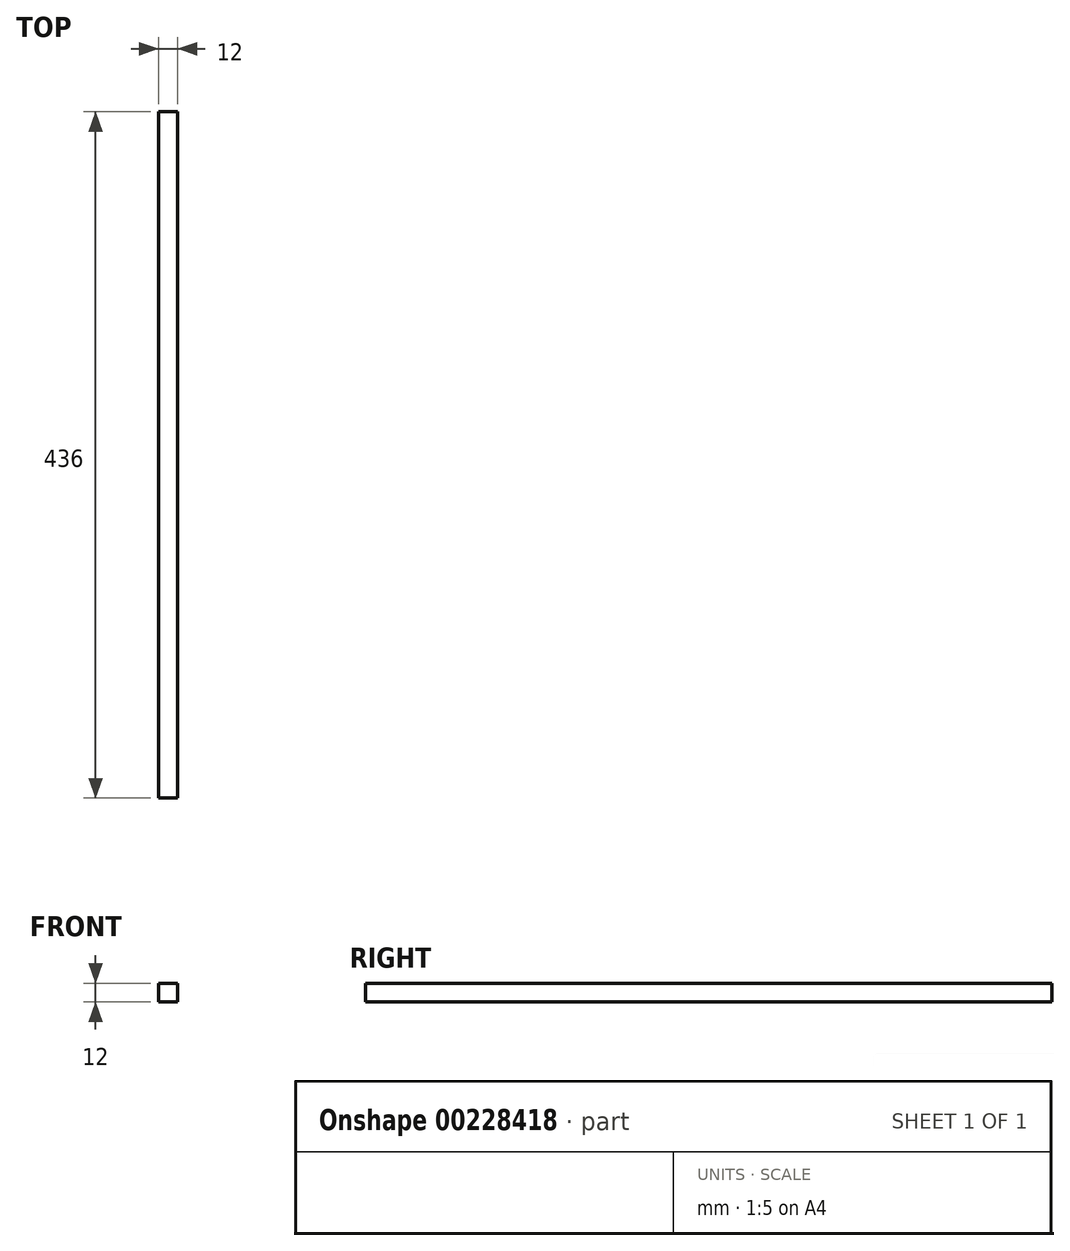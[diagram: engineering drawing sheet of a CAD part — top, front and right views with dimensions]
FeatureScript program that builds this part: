
annotation { "Feature Type Name" : "Feature", "Feature Type Description" : "" }
export const myFeature = defineFeature(function(context is Context, id is Id, definition is map)
    precondition{}
    {
        {
            var Q0;
            Q0=qCreatedBy(makeId("Front.planeOp"),FACE);
            var sketch = newSketch(context, id + "F0", { "sketchPlane" : qUnion([Q0])});
            skLineSegment(sketch, "E0.bottom", {"start": v(-14.67, 12) * mm, "end": v(-2.67, 12) * mm});
            skLineSegment(sketch, "E0.top", {"start": v(-14.67, 0) * mm, "end": v(-2.67, 0) * mm});
            skLineSegment(sketch, "E0.left", {"start": v(-14.67, 12) * mm, "end": v(-14.67, 0) * mm});
            skLineSegment(sketch, "E0.right", {"start": v(-2.67, 12) * mm, "end": v(-2.67, 0) * mm});
            skSolve(sketch);
        }
        {
            var Q0;
            Q0 = qSketchRegion(id + "F0", true);
            extrude(context, id + "F1", {"entities" : qUnion([Q0]), "depth" : 436 * mm});
        }
    });
